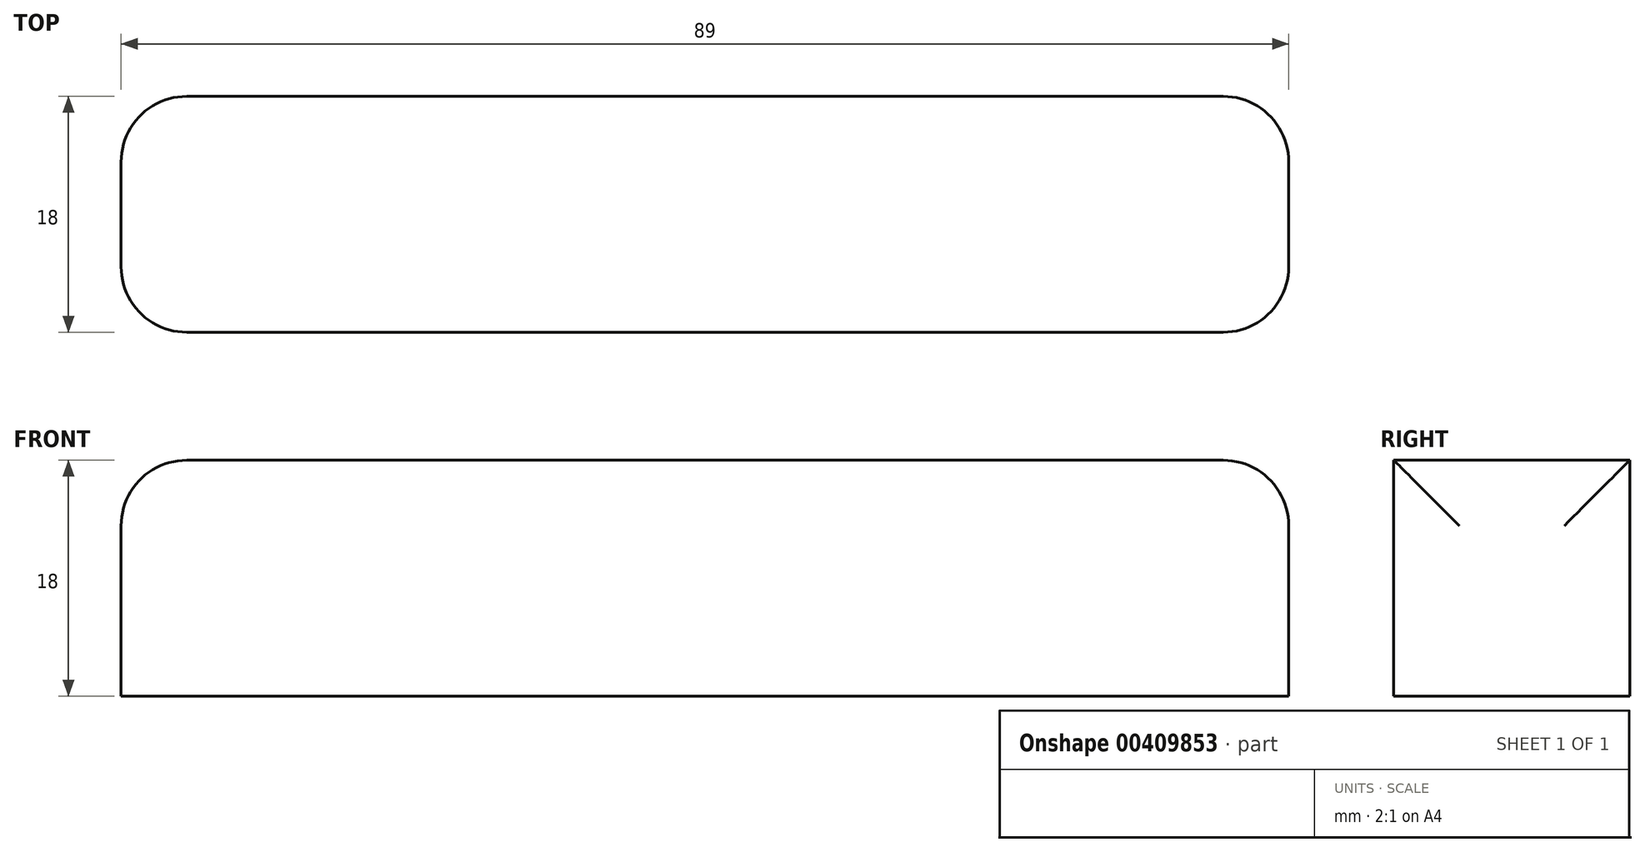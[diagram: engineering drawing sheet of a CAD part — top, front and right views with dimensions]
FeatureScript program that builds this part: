
annotation { "Feature Type Name" : "Feature", "Feature Type Description" : "" }
export const myFeature = defineFeature(function(context is Context, id is Id, definition is map)
    precondition{}
    {
        {
            var Q0;
            Q0=qCreatedBy(makeId("Top.planeOp"),FACE);
            var sketch = newSketch(context, id + "F0", { "sketchPlane" : qUnion([Q0])});
            skLineSegment(sketch, "E0", {"start": v(0, 0) * mm, "end": v(89, 0) * mm});
            skLineSegment(sketch, "E1", {"start": v(89, 0) * mm, "end": v(89, 18) * mm});
            skLineSegment(sketch, "E2", {"start": v(89, 18) * mm, "end": v(0, 18) * mm});
            skLineSegment(sketch, "E3", {"start": v(0, 18) * mm, "end": v(0, 0) * mm});
            skSolve(sketch);
        }
        {
            var Q0;
            Q0 = qSketchRegion(id + "F0", true);
            extrude(context, id + "F1", {"entities" : qUnion([Q0]), "depth" : 18 * mm});
        }
        {
            var Q0;
            Q0=makeQuery(id+"F1.opExtrude","SWEPT_EDGE",EDGE,{"disambiguationData":[OSD([sQuery(id+"F0.wireOp",EDGE,"E0"),sQuery(id+"F0.wireOp",EDGE,"E3")])]});
            var Q1;
            Q1=makeQuery(id+"F1.opExtrude","SWEPT_EDGE",EDGE,{"disambiguationData":[OSD([sQuery(id+"F0.wireOp",EDGE,"E0"),sQuery(id+"F0.wireOp",EDGE,"E1")])]});
            var Q2;
            Q2=makeQuery(id+"F1.opExtrude","SWEPT_EDGE",EDGE,{"disambiguationData":[OSD([sQuery(id+"F0.wireOp",EDGE,"E1"),sQuery(id+"F0.wireOp",EDGE,"E2")])]});
            var Q3;
            Q3=makeQuery(id+"F1.opExtrude","SWEPT_EDGE",EDGE,{"disambiguationData":[OSD([sQuery(id+"F0.wireOp",EDGE,"E2"),sQuery(id+"F0.wireOp",EDGE,"E3")])]});
            var Q4;
            Q4=makeQuery(id+"F1.opExtrude","CAP_EDGE",EDGE,{"disambiguationData":[OSD([sQuery(id+"F0.wireOp",EDGE,"E3")])],"isStart":false});
            var Q5;
            Q5=makeQuery(id+"F1.opExtrude","CAP_EDGE",EDGE,{"disambiguationData":[OSD([sQuery(id+"F0.wireOp",EDGE,"E1")])],"isStart":false});
            fillet(context, id + "F2", {"entities" : qUnion([Q0, Q1, Q2, Q3, Q4, Q5]), "radius" : 5 * mm, "tangentPropagation" : true, "allowEdgeOverflow" : false});
        }
    });
